# Revit family: BDG_BossDesign_Tbls_Axis1
name_source: partatom
category: Furniture
revit_build: Autodesk Revit 2015 (Build: 20140903_1530(x64)
units: mm (PartAtom-declared; Revit-internal decimal feet)

## types (10) — shared parameters
Assembly Code = E2020200
AssetType = Moveable
BIMObjectName = BDG_BossDesign_Tables_Axis
Category = Pr_40_50_21 Desks, tables and worktops
CodePerformance = ANSI BIFMA X5.1
DurationUnit = year
ExpectedLife = 5
IfcExportAs = IfcFurnishingElementType
IfcExportType = TABLE
Keynote = Pr_40_50_21
ManufacturerName = Boss Design
ManufacturerURL = www.boss-design.co.uk
Material = Aluminium
NBSDescription = Tables
NBSReference = 45-35-86/327
Name = Tables_Axis_BossDesign
ProductInformation = www.bossdesign.com/product-list/axis/
Shape = Circular
SustainabilityPerformance = 100% Recyclable
URL = www.boss-design.co.uk
Uniclass2015Description = Desks, tables and worktops
Uniclass2015Reference = Pr_40_50_21
Uniclass2015Version = Products v1.6
Version = 1
WarrantyDescription = Structural Warranty Excludes Foams and Fabrics
WarrantyDurationLabor = 5
WarrantyDurationParts = 5
WarrantyDurationUnit = year
zero-valued in all types: NumberOfChairs, WorksurfaceArea

## per-type parameters (varying)
| type | Description | Features | Finish | Model | ModelNumber | ModelReference | NominalHeight | NominalLength | NominalWidth | Radius | Size | TableEdgeMaterial | TableTopMaterial |
| 800mm dia 400mm High Coffee White MFC | White MFC Axis 400mm High 800mm dia Table | Melamine Top | White MFC | AXT1 | AXT1 | White MFC Axis 400mm High 800mm dia Table | 400 mm  [stored 1.31234 ft] | 800 mm  [stored 2.62467 ft] | 800 mm  [stored 2.62467 ft] | 400 mm  [stored 1.31234 ft] | 800 x 800 x 400mm | BDG_Generic_MFC_Black | BDG_Generic_MFC_White |
| 800mm dia 400mm High Coffee BAW Veneer | Black American Walnut Veneer Axis 400mm High 800mm dia Table | Veneer Top | Black American Walnut Veneer | AXT2 | AXT2 | Black American Walnut Veneer Axis 400mm High 800mm dia Table | 400 mm  [stored 1.31234 ft] | 800 mm  [stored 2.62467 ft] | 800 mm  [stored 2.62467 ft] | 400 mm  [stored 1.31234 ft] | 800 x 800 x 400mm | BDG_Generic_WoodVeneer_Walnut_BlackAmerican | BDG_Generic_WoodVeneer_Walnut_BlackAmerican |
| 800mm dia 740mm High Meeting White MFC | White MFC Axis 740mm High 800mm dia Table | Melamine Top | White MFC | AXT5 | AXT5 | White MFC Axis 740mm High 800mm dia Table | 740 mm  [stored 2.42782 ft] | 800 mm  [stored 2.62467 ft] | 800 mm  [stored 2.62467 ft] | 400 mm  [stored 1.31234 ft] | 800 x 800 x 740mm | BDG_Generic_MFC_Black | BDG_Generic_MFC_White |
| 800mm dia 740mm High Meeting BAW Veneer | Black American Walnut Veneer Axis 740mm High 800mm dia Table | Veneer Top | Black American Walnut Veneer | AXT6 | AXT6 | Black American Walnut Veneer Axis 740mm High 800mm dia Table | 740 mm  [stored 2.42782 ft] | 800 mm  [stored 2.62467 ft] | 800 mm  [stored 2.62467 ft] | 400 mm  [stored 1.31234 ft] | 800 x 800 x 740mm | BDG_Generic_WoodVeneer_Walnut_BlackAmerican | BDG_Generic_WoodVeneer_Walnut_BlackAmerican |
| 800mm dia 950mm High Meeting White MFC | White MFC Axis 950mm High 800mm dia Table | Melamine Top | White MFC | AXT7 | AXT7 | White MFC Axis 950mm High 800mm dia Table | 950 mm  [stored 3.1168 ft] | 800 mm  [stored 2.62467 ft] | 800 mm  [stored 2.62467 ft] | 400 mm  [stored 1.31234 ft] | 800 x 800 x 950mm | BDG_Generic_MFC_Black | BDG_Generic_MFC_White |
| 800mm dia 950mm High Meeting BAW Veneer | Black American Walnut Veneer Axis 950mm High 800mm dia Table | Veneer Top | Black American Walnut Veneer | AXT8 | AXT8 | Black American Walnut Veneer Axis 950mm High 800mm dia Table | 950 mm  [stored 3.1168 ft] | 800 mm  [stored 2.62467 ft] | 800 mm  [stored 2.62467 ft] | 400 mm  [stored 1.31234 ft] | 800 x 800 x 950mm | BDG_Generic_WoodVeneer_Walnut_BlackAmerican | BDG_Generic_WoodVeneer_Walnut_BlackAmerican |
| 1000mm dia 400mm High Coffee White MFC | White MFC Axis 400mm High 1000mm dia Table | Melamine Top | White MFC | AXT9 | AXT9 | White MFC Axis 400mm High 1000mm dia Table | 400 mm  [stored 1.31234 ft] | 1000 mm  [stored 3.28084 ft] | 1000 mm  [stored 3.28084 ft] | 500 mm  [stored 1.64042 ft] | 1000 x 1000 x 400mm | BDG_Generic_MFC_Black | BDG_Generic_MFC_White |
| 1000mm dia 400mm High Coffee BAW Veneer | Black American Walnut Veneer Axis 400mm High 1000mm dia Table | Veneer Top | Black American Walnut Veneer | AXT10 | AXT10 | Black American Walnut Veneer Axis 400mm High 1000mm dia Table | 400 mm  [stored 1.31234 ft] | 1000 mm  [stored 3.28084 ft] | 1000 mm  [stored 3.28084 ft] | 500 mm  [stored 1.64042 ft] | 1000 x 1000 x 400mm | BDG_Generic_WoodVeneer_Walnut_BlackAmerican | BDG_Generic_WoodVeneer_Walnut_BlackAmerican |
| 1000mm dia 740mm High Meeting White MFC | White MFC Axis 740mm High 1000mm dia Table | Melamine Top | White MFC | AXT13 | AXT13 | White MFC Axis 740mm High 1000mm dia Table | 740 mm  [stored 2.42782 ft] | 1000 mm  [stored 3.28084 ft] | 1000 mm  [stored 3.28084 ft] | 500 mm  [stored 1.64042 ft] | 1000 x 1000 x 740mm | BDG_Generic_MFC_Black | BDG_Generic_MFC_White |
| 1000mm dia 740mm High Meeting BAW Veneer | Black American Walnut Veneer Axis 740mm High 1000mm dia Table | Veneer Top | Black American Walnut Veneer | AXT14 | AXT14 | Black American Walnut Veneer Axis 740mm High 1000mm dia Table | 740 mm  [stored 2.42782 ft] | 1000 mm  [stored 3.28084 ft] | 1000 mm  [stored 3.28084 ft] | 500 mm  [stored 1.64042 ft] | 1000 x 1000 x 740mm | BDG_Generic_WoodVeneer_Walnut_BlackAmerican | BDG_Generic_WoodVeneer_Walnut_BlackAmerican |

note: [stored X ft] marks values corroborated as IEEE doubles in the binary element streams (Revit-internal decimal feet)

## geometry (parser evidence)
native form markers: Blend x242, Sweep x1
no freeform markers — native parametric forms only
